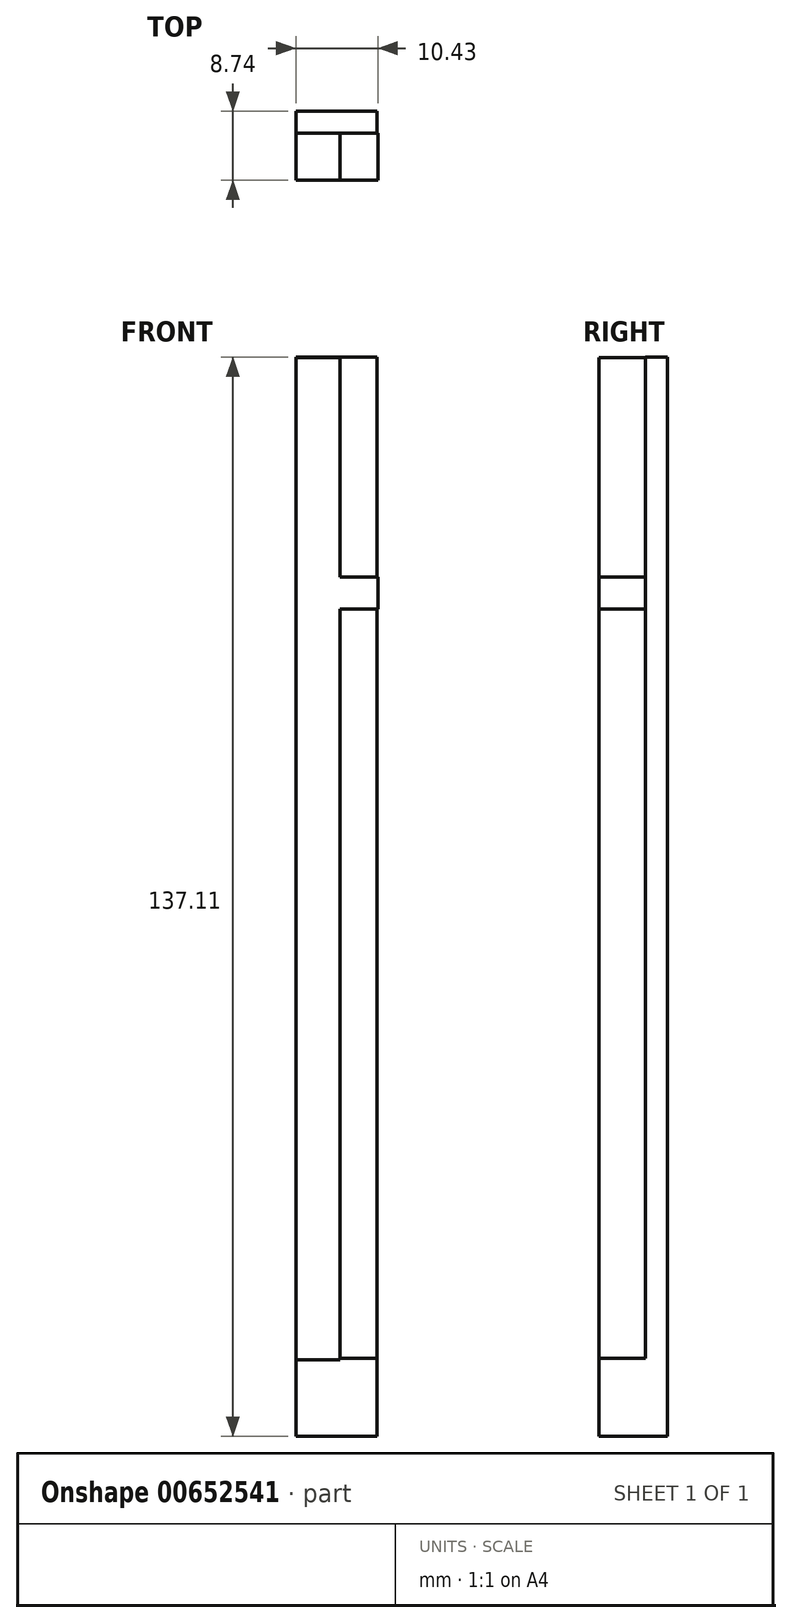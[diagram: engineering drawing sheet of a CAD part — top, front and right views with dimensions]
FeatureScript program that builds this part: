
annotation { "Feature Type Name" : "Feature", "Feature Type Description" : "" }
export const myFeature = defineFeature(function(context is Context, id is Id, definition is map)
    precondition{}
    {
        {
            var Q0;
            Q0=qCreatedBy(makeId("Front.planeOp"),FACE);
            var sketch = newSketch(context, id + "F0", { "sketchPlane" : qUnion([Q0])});
            skLineSegment(sketch, "E0.bottom", {"start": v(-4.7, 92.98) * mm, "end": v(5.6, 92.98) * mm});
            skLineSegment(sketch, "E0.top", {"start": v(-4.7, -34.22) * mm, "end": v(5.6, -34.22) * mm});
            skLineSegment(sketch, "E0.left", {"start": v(-4.7, 92.98) * mm, "end": v(-4.7, -34.22) * mm});
            skLineSegment(sketch, "E0.right", {"start": v(5.6, 92.98) * mm, "end": v(5.6, -34.22) * mm});
            skSolve(sketch);
        }
        {
            var Q0;
            Q0=makeQuery(id+"F0.imprint","IMPRINT",FACE,{"disambiguationData":[TD([[makeQuery(id+"F0.imprint","IMPRINT",EDGE,{"derivedFrom":sQuery(id+"F0.wireOp",EDGE,"E0.bottom")}),-1.0]])]});
            extrude(context, id + "F1", {"entities" : qUnion([Q0]), "oppositeDirection" : true, "depth" : 2.8 * mm, "offsetDistance" : 25.4 * mm});
        }
        {
            var Q0;
            Q0=qCreatedBy(makeId("Right.planeOp"),FACE);
            var sketch = newSketch(context, id + "F2", { "sketchPlane" : qUnion([Q0])});
            skLineSegment(sketch, "E1.bottom", {"start": v(0, 92.93) * mm, "end": v(8.74, 92.93) * mm});
            skLineSegment(sketch, "E1.top", {"start": v(0, -34.42) * mm, "end": v(8.74, -34.42) * mm});
            skLineSegment(sketch, "E1.left", {"start": v(0, 92.93) * mm, "end": v(0, -34.42) * mm});
            skLineSegment(sketch, "E1.right", {"start": v(8.74, 92.93) * mm, "end": v(8.74, -34.42) * mm});
            skSolve(sketch);
        }
        {
            var Q0;
            Q0=qSketchRegion(id+"F2",true);
            extrude(context, id + "F3", {"entities" : qUnion([Q0]), "operationType" : NewBodyOperationType.ADD, "depth" : 5.6 * mm, "offsetDistance" : 25.4 * mm});
        }
        {
            var Q0;
            Q0=makeQuery(id+"F1.opExtrude","SWEPT_FACE",FACE,{"disambiguationData":[OSD([sQuery(id+"F0.wireOp",EDGE,"E0.top")])]});
            var sketch = newSketch(context, id + "F4", { "sketchPlane" : qUnion([Q0])});
            skLineSegment(sketch, "E2.bottom", {"start": v(5.6, 0) * mm, "end": v(-4.7, 0) * mm});
            skLineSegment(sketch, "E2.top", {"start": v(5.6, -8.73) * mm, "end": v(-4.7, -8.73) * mm});
            skLineSegment(sketch, "E2.left", {"start": v(5.6, 0) * mm, "end": v(5.6, -8.73) * mm});
            skLineSegment(sketch, "E2.right", {"start": v(-4.7, 0) * mm, "end": v(-4.7, -8.73) * mm});
            skSolve(sketch);
        }
        {
            var Q0;
            Q0=qSketchRegion(id+"F4",true);
            extrude(context, id + "F5", {"entities" : qUnion([Q0]), "operationType" : NewBodyOperationType.ADD, "depth" : 9.9 * mm, "offsetDistance" : 25.4 * mm});
        }
        {
            var Q0;
            Q0=makeQuery(id+"F3.opExtrude","CAP_FACE",FACE,{"disambiguationData":[OSD([sQuery(id+"F2.wireOp",EDGE,"E1.bottom"),sQuery(id+"F2.wireOp",EDGE,"E1.top"),sQuery(id+"F2.wireOp",EDGE,"E1.left"),sQuery(id+"F2.wireOp",EDGE,"E1.right")])],"isStart":true});
            var sketch = newSketch(context, id + "F6", { "sketchPlane" : qUnion([Q0])});
            skLineSegment(sketch, "E3.bottom", {"start": v(-8.74, 65.01) * mm, "end": v(-2.8, 65.01) * mm});
            skLineSegment(sketch, "E3.top", {"start": v(-8.74, 61) * mm, "end": v(-2.8, 61) * mm});
            skLineSegment(sketch, "E3.left", {"start": v(-8.74, 65.01) * mm, "end": v(-8.74, 61) * mm});
            skLineSegment(sketch, "E3.right", {"start": v(-2.8, 65.01) * mm, "end": v(-2.8, 61) * mm});
            skSolve(sketch);
        }
        {
            var Q0;
            Q0=qSketchRegion(id+"F6",true);
            extrude(context, id + "F7", {"entities" : qUnion([Q0]), "operationType" : NewBodyOperationType.ADD, "depth" : 4.83 * mm, "offsetDistance" : 25.4 * mm});
        }
        {
            var Q0;
            Q0=makeQuery(id+"F1.opExtrude","SWEPT_BODY",BODY,{"disambiguationData":[OSD([sQuery(id+"F0.wireOp",EDGE,"E0.bottom"),sQuery(id+"F0.wireOp",EDGE,"E0.top"),sQuery(id+"F0.wireOp",EDGE,"E0.left"),sQuery(id+"F0.wireOp",EDGE,"E0.right")])]});
            var Q1;
            Q1=makeQuery(id+"F5.opExtrude","SWEPT_EDGE",EDGE,{"disambiguationData":[OSD([sQuery(id+"F4.wireOp",EDGE,"E2.bottom"),sQuery(id+"F4.wireOp",EDGE,"E2.right")])]});
            transform(context, id + "F8", {"entities" : qUnion([Q0]), "transformType" : TransformType.ROTATION, "transformAxis" : qUnion([Q1]), "angle" : 180 * degree, "oppositeDirection" : true, "makeCopy" : false});
        }
    });
